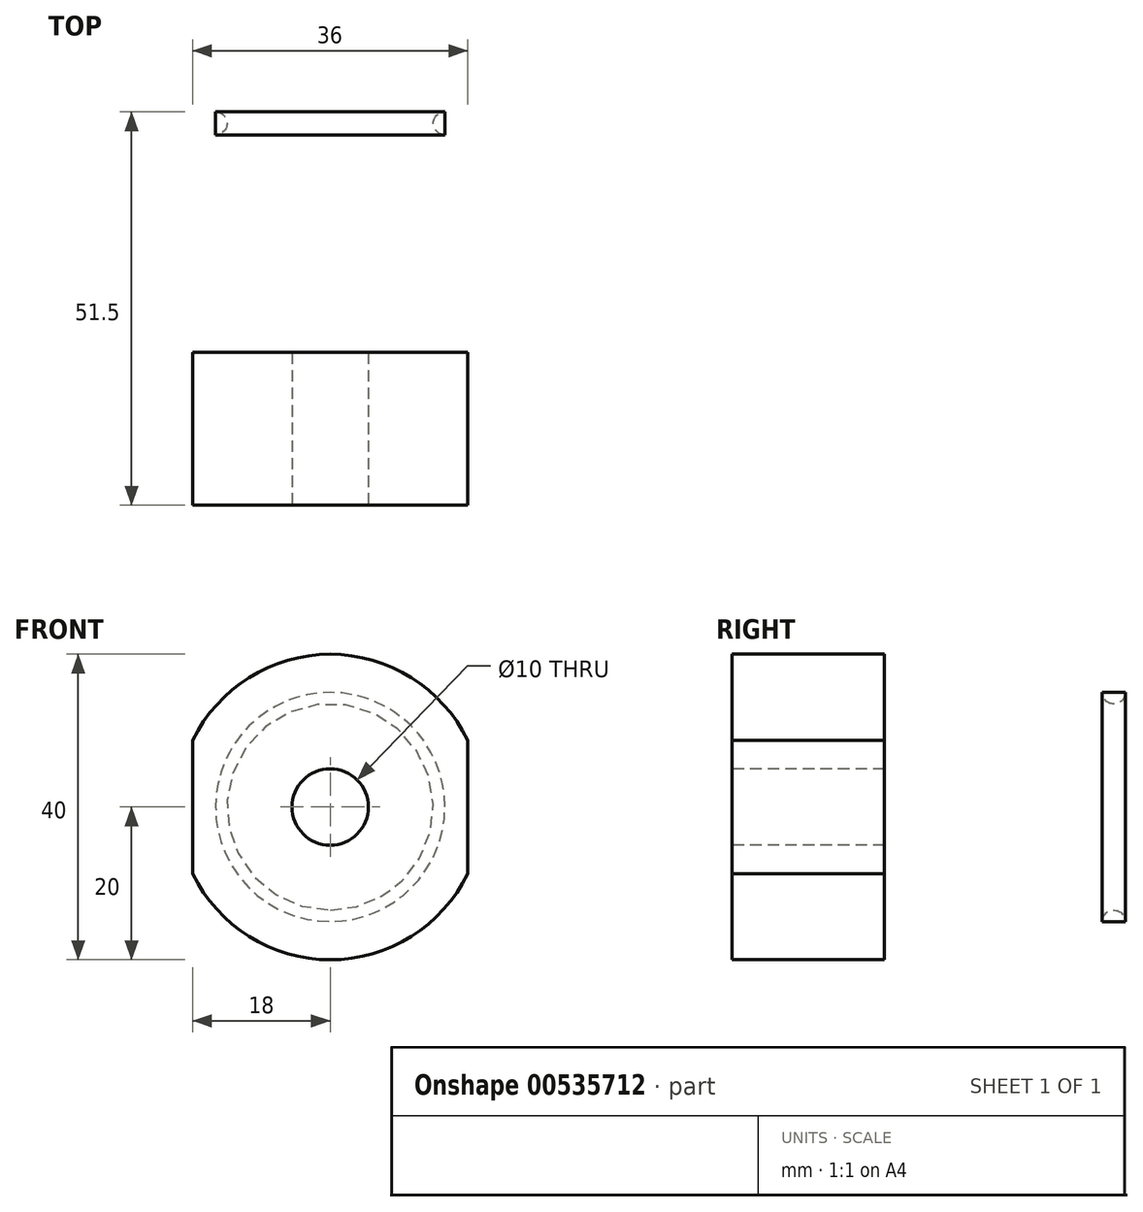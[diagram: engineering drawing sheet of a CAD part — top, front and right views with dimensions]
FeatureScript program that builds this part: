
annotation { "Feature Type Name" : "Feature", "Feature Type Description" : "" }
export const myFeature = defineFeature(function(context is Context, id is Id, definition is map)
    precondition{}
    {
        {
            var Q0;
            Q0=qCreatedBy(makeId("Front.planeOp"),FACE);
            var sketch = newSketch(context, id + "F0", { "sketchPlane" : qUnion([Q0])});
            skCircle(sketch, "E0", {"center": v(0, 0) * mm, "radius": 20 * mm});
            skLineSegment(sketch, "E1", {"start": v(0, 0) * mm, "end": v(18, 0) * mm});
            skLineSegment(sketch, "E2", {"start": v(18, 0) * mm, "end": v(18, 8.72) * mm});
            skLineSegment(sketch, "E3", {"start": v(18, 8.72) * mm, "end": v(18, -8.72) * mm});
            skLineSegment(sketch, "E4", {"start": v(0, 0) * mm, "end": v(-18, 0) * mm});
            skLineSegment(sketch, "E5", {"start": v(-18, 0) * mm, "end": v(-18, 8.72) * mm});
            skLineSegment(sketch, "E6", {"start": v(-18, 8.72) * mm, "end": v(-18, -8.72) * mm});
            skSolve(sketch);
        }
        {
            var Q0;
            {var subQ1=sQuery(id+"F0.wireOp",EDGE,"E1");Q0=makeQuery(id+"F0.imprint","IMPRINT",FACE,{"disambiguationData":[TD([[makeQuery(id+"F0.imprint","IMPRINT",EDGE,{"derivedFrom":subQ1}),1.0]])]});}
            var Q1;
            {var subQ1=sQuery(id+"F0.wireOp",EDGE,"E1");Q1=makeQuery(id+"F0.imprint","IMPRINT",FACE,{"disambiguationData":[TD([[makeQuery(id+"F0.imprint","IMPRINT",EDGE,{"derivedFrom":subQ1}),-1.0]])]});}
            extrude(context, id + "F1", {"entities" : qUnion([Q0, Q1]), "depth" : 20 * mm, "offsetDistance" : 25 * mm});
        }
        {
            var Q0;
            {var subQ1=sQuery(id+"F0.wireOp",EDGE,"E1");Q0=makeQuery(id+"F0.imprint","IMPRINT",FACE,{"disambiguationData":[TD([[makeQuery(id+"F0.imprint","IMPRINT",EDGE,{"derivedFrom":subQ1}),1.0]])]});}
            var sketch = newSketch(context, id + "F2", { "sketchPlane" : qUnion([Q0])});
            skCircle(sketch, "E7", {"center": v(0, 0) * mm, "radius": 15 * mm});
            skSolve(sketch);
        }
        {
            var Q0;
            Q0 = qSketchRegion(id + "F2", true);
            extrude(context, id + "F3", {"entities" : qUnion([Q0]), "operationType" : NewBodyOperationType.ADD, "oppositeDirection" : true, "depth" : 40 * mm, "offsetDistance" : 25 * mm});
        }
        {
            var Q0;
            Q0=qCreatedBy(makeId("Front.planeOp"),FACE);
            var sketch = newSketch(context, id + "F4", { "sketchPlane" : qUnion([Q0])});
            skCircle(sketch, "E8", {"center": v(0, 0) * mm, "radius": 5 * mm});
            skSolve(sketch);
        }
        {
            var Q0;
            Q0 = qSketchRegion(id + "F4", true);
            extrude(context, id + "F5", {"entities" : qUnion([Q0]), "operationType" : NewBodyOperationType.REMOVE, "endBound" : BoundingType.UP_TO_NEXT, "oppositeDirection" : true, "depth" : 25 * mm, "offsetDistance" : 25 * mm});
        }
        {
            var Q0;
            Q0 = qSketchRegion(id + "F4", true);
            extrude(context, id + "F6", {"entities" : qUnion([Q0]), "operationType" : NewBodyOperationType.REMOVE, "endBound" : BoundingType.UP_TO_NEXT, "depth" : 25 * mm, "offsetDistance" : 25 * mm});
        }
        {
            var Q0;
            Q0=qCreatedBy(makeId("Right.planeOp"),FACE);
            var sketch = newSketch(context, id + "F7", { "sketchPlane" : qUnion([Q0])});
            skLineSegment(sketch, "E9.bottom", {"start": v(0, 0) * mm, "end": v(40, 0) * mm});
            skLineSegment(sketch, "E9.top", {"start": v(0, 15) * mm, "end": v(40, 15) * mm});
            skLineSegment(sketch, "E9.left", {"start": v(0, 0) * mm, "end": v(0, 15) * mm});
            skLineSegment(sketch, "E9.right", {"start": v(40, 0) * mm, "end": v(40, 15) * mm});
            skLineSegment(sketch, "E10", {"start": v(40, 15) * mm, "end": v(30, 15) * mm});
            skCircle(sketch, "E11", {"center": v(30, 15) * mm, "radius": 1.5 * mm});
            skLineSegment(sketch, "E12", {"start": v(39, 15) * mm, "end": v(40, 14) * mm});
            skLineSegment(sketch, "E13", {"start": v(39, 15) * mm, "end": v(40, 15) * mm});
            skLineSegment(sketch, "E14", {"start": v(40, 14) * mm, "end": v(40, 15) * mm});
            skSolve(sketch);
        }
        {
            var Q0;
            {var subQ0=sQuery(id+"F7.wireOp",EDGE,"E10");var subQ1=sQuery(id+"F7.wireOp",EDGE,"E9.top");var subQ2=makeQuery(id+"F7.imprint","INTERSECT",VERTEX,{"derivedFrom":[subQ1,subQ0]});Q0=makeQuery(id+"F7.imprint","IMPRINT",FACE,{"disambiguationData":[TD([[makeQuery(id+"F7.imprint","IMPRINT",EDGE,{"disambiguationData":[TD([[subQ2,1.0]])],"derivedFrom":subQ1}),-1.0]])]});}
            var Q1;
            Q1=makeQuery(id+"F3.opExtrude","SWEPT_FACE",FACE,{"disambiguationData":[OSD([sQuery(id+"F2.wireOp",EDGE,"E7")])]});
            revolve(context, id + "F8", {"operationType" : NewBodyOperationType.REMOVE, "entities" : qUnion([Q0]), "axis" : qUnion([Q1]), "revolveType" : RevolveType.FULL, "oppositeDirection" : true});
        }
        {
            var Q0;
            Q0=makeQuery(id+"F7.imprint","IMPRINT",FACE,{"disambiguationData":[TD([[makeQuery(id+"F7.imprint","IMPRINT",EDGE,{"derivedFrom":sQuery(id+"F7.wireOp",EDGE,"E12")}),1.0]])]});
            var Q1;
            {var subQ0=sQuery(id+"F2.wireOp",EDGE,"E7");Q1=makeQuery(id+"F8.boolean.opBoolean","SPLIT",FACE,{"disambiguationData":[TD([makeQuery(id+"F3.opExtrude","CAP_FACE",FACE,{"disambiguationData":[OSD([subQ0])],"isStart":false})])],"derivedFrom":makeQuery(id+"F3.opExtrude","SWEPT_FACE",FACE,{"disambiguationData":[OSD([subQ0])]})});}
            revolve(context, id + "F9", {"operationType" : NewBodyOperationType.REMOVE, "entities" : qUnion([Q0]), "axis" : qUnion([Q1]), "revolveType" : RevolveType.FULL, "oppositeDirection" : true});
        }
    });
